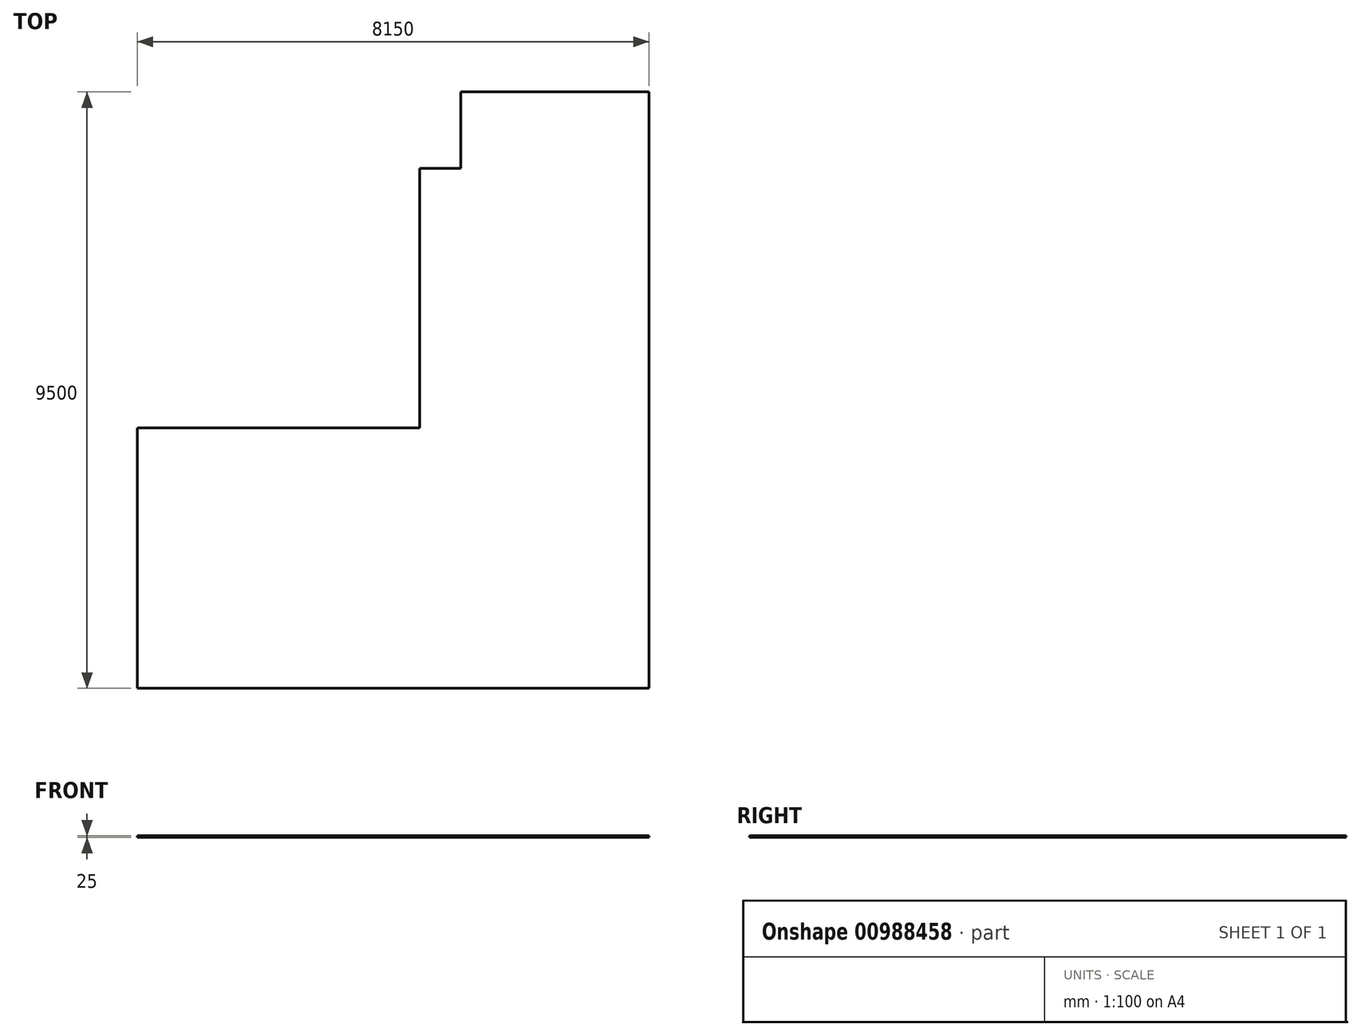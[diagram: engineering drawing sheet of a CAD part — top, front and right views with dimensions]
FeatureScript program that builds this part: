
annotation { "Feature Type Name" : "Feature", "Feature Type Description" : "" }
export const myFeature = defineFeature(function(context is Context, id is Id, definition is map)
    precondition{}
    {
        {
            var Q0;
            Q0=qCreatedBy(makeId("Top.planeOp"),FACE);
            var sketch = newSketch(context, id + "F0", { "sketchPlane" : qUnion([Q0])});
            skLineSegment(sketch, "E0", {"start": v(-1500, 5350) * mm, "end": v(1500, 5350) * mm});
            skLineSegment(sketch, "E1", {"start": v(1500, 5350) * mm, "end": v(1500, -4150) * mm});
            skLineSegment(sketch, "E2", {"start": v(1500, -4150) * mm, "end": v(-6650, -4150) * mm});
            skLineSegment(sketch, "E3", {"start": v(-1500, 5350) * mm, "end": v(-1500, 4130) * mm});
            skLineSegment(sketch, "E4", {"start": v(-1500, 4130) * mm, "end": v(-2150, 4130) * mm});
            skLineSegment(sketch, "E5", {"start": v(-2150, 4130) * mm, "end": v(-2150, 0) * mm});
            skLineSegment(sketch, "E6", {"start": v(-2150, 0) * mm, "end": v(-6650, 0) * mm});
            skLineSegment(sketch, "E7", {"start": v(-6650, 0) * mm, "end": v(-6650, -4150) * mm});
            skSolve(sketch);
        }
        {
            var Q0;
            Q0=makeQuery(id+"F0.imprint","IMPRINT",FACE,{"disambiguationData":[TD([[makeQuery(id+"F0.imprint","IMPRINT",EDGE,{"derivedFrom":sQuery(id+"F0.wireOp",EDGE,"E0")}),-1.0]])]});
            extrude(context, id + "F1", {"entities" : qUnion([Q0]), "depth" : 25 * mm, "offsetDistance" : 25 * mm});
        }
    });
